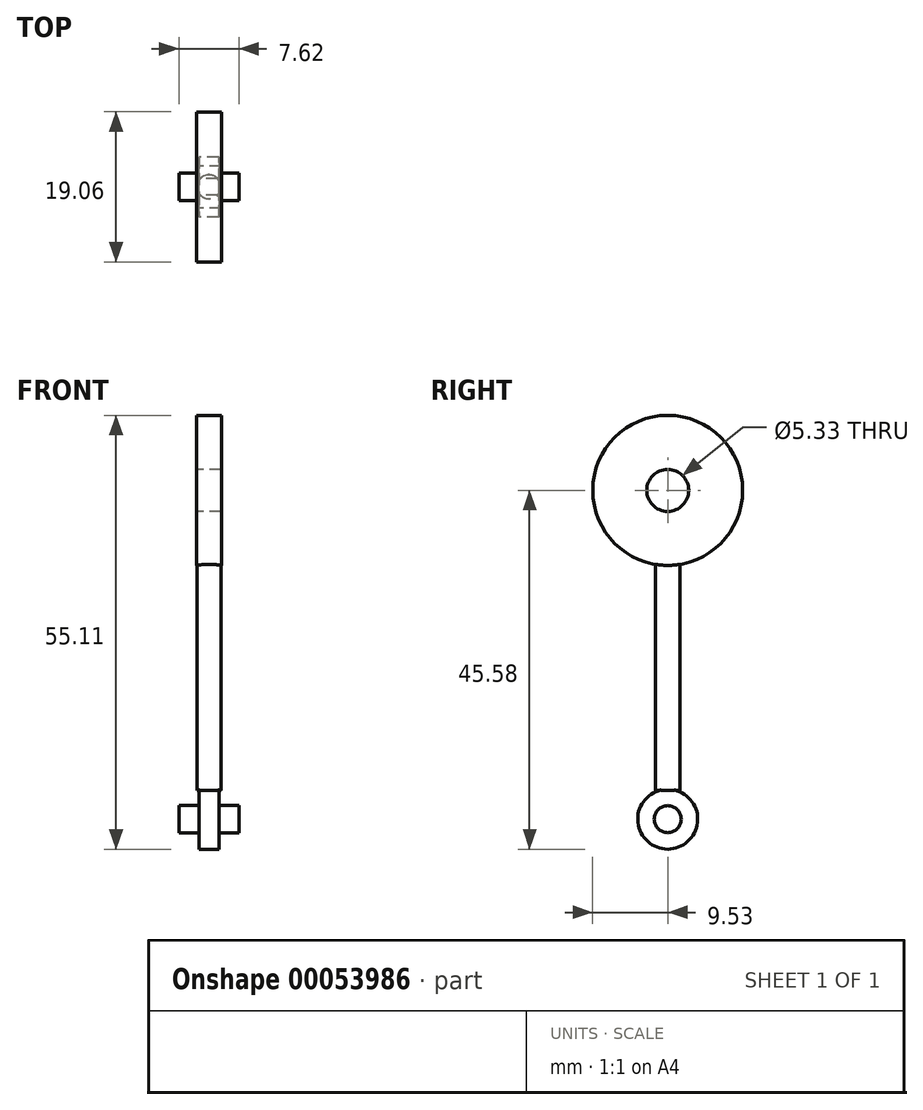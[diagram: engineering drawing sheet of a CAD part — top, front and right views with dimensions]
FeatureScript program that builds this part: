
annotation { "Feature Type Name" : "Feature", "Feature Type Description" : "" }
export const myFeature = defineFeature(function(context is Context, id is Id, definition is map)
    precondition{}
    {
        {
            var Q0;
            Q0=qCreatedBy(makeId("Right.planeOp"),FACE);
            var sketch = newSketch(context, id + "F0", { "sketchPlane" : qUnion([Q0])});
            skCircle(sketch, "E0", {"center": v(0, 0) * mm, "radius": 9.53 * mm});
            skCircle(sketch, "E1", {"center": v(0, 0) * mm, "radius": 2.67 * mm});
            skSolve(sketch);
        }
        {
            var Q0;
            Q0=makeQuery(id+"F0.imprint","IMPRINT",FACE,{"disambiguationData":[TD([[makeQuery(id+"F0.imprint","IMPRINT",EDGE,{"derivedFrom":sQuery(id+"F0.wireOp",EDGE,"E0")}),1.0]])]});
            extrude(context, id + "F1", {"entities" : qUnion([Q0]), "endBound" : BoundingType.SYMMETRIC, "depth" : 3.17 * mm});
        }
        {
            var Q0;
            Q0=qCreatedBy(makeId("Top.planeOp"),FACE);
            var sketch = newSketch(context, id + "F2", { "sketchPlane" : qUnion([Q0])});
            skCircle(sketch, "E2", {"center": v(0, 0) * mm, "radius": 1.53 * mm});
            skSolve(sketch);
        }
        {
            var Q0;
            Q0 = qSketchRegion(id + "F2", true);
            extrude(context, id + "F3", {"entities" : qUnion([Q0]), "operationType" : NewBodyOperationType.ADD, "oppositeDirection" : true, "depth" : 38.1 * mm, "hasSecondDirection" : true, "secondDirectionOppositeDirection" : true, "secondDirectionDepth" : 5.08 * mm});
        }
        {
            var Q0;
            Q0=qCreatedBy(makeId("Right.planeOp"),FACE);
            var sketch = newSketch(context, id + "F4", { "sketchPlane" : qUnion([Q0])});
            skCircle(sketch, "E3", {"center": v(0, -41.77) * mm, "radius": 3.81 * mm});
            skSolve(sketch);
        }
        {
            var Q0;
            Q0 = qSketchRegion(id + "F4", true);
            extrude(context, id + "F5", {"entities" : qUnion([Q0]), "operationType" : NewBodyOperationType.ADD, "endBound" : BoundingType.SYMMETRIC, "depth" : 2.54 * mm});
        }
        {
            var Q0;
            Q0=makeQuery(id+"F5.opExtrude","CAP_FACE",FACE,{"disambiguationData":[OSD([sQuery(id+"F4.wireOp",EDGE,"E3")])],"isStart":true});
            var sketch = newSketch(context, id + "F6", { "sketchPlane" : qUnion([Q0])});
            skCircle(sketch, "E4", {"center": v(0, -41.77) * mm, "radius": 1.72 * mm});
            skSolve(sketch);
        }
        {
            var Q0;
            Q0=makeQuery(id+"F6.imprint","IMPRINT",FACE,{"disambiguationData":[TD([[makeQuery(id+"F6.imprint","IMPRINT",EDGE,{"derivedFrom":sQuery(id+"F6.wireOp",EDGE,"E4")}),1.0]])]});
            extrude(context, id + "F7", {"entities" : qUnion([Q0]), "operationType" : NewBodyOperationType.ADD, "depth" : 2.54 * mm, "hasSecondDirection" : true, "secondDirectionOppositeDirection" : true, "secondDirectionDepth" : 5.08 * mm});
        }
    });
